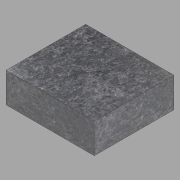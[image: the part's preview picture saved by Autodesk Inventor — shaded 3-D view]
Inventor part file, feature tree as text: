
AUTODESK INVENTOR PART (.ipt)
format: ipt  version: 2022.2 (Build 262287000, 287)  size: 119,808 bytes
history: native  units: in
note: dims shown in document units (in); Inventor stores cm internally (conversion verified against a paired STEP export)
features: other x1, extrude x1, sketch x1
ambient origin geometry x8: Origin, YZ Plane, XZ Plane, XY Plane, X Axis, Y Axis, Z Axis, Center Point
bodies: Solid1 (feature_tree)
feature tree (3):
  other  "Test"
  extrude  "Extrusion1"  Depth=16.25in
  sketch  "Sketch1"  dims[d0=18.0in d1=16.25in d2=6.125in d3=0.0in]
